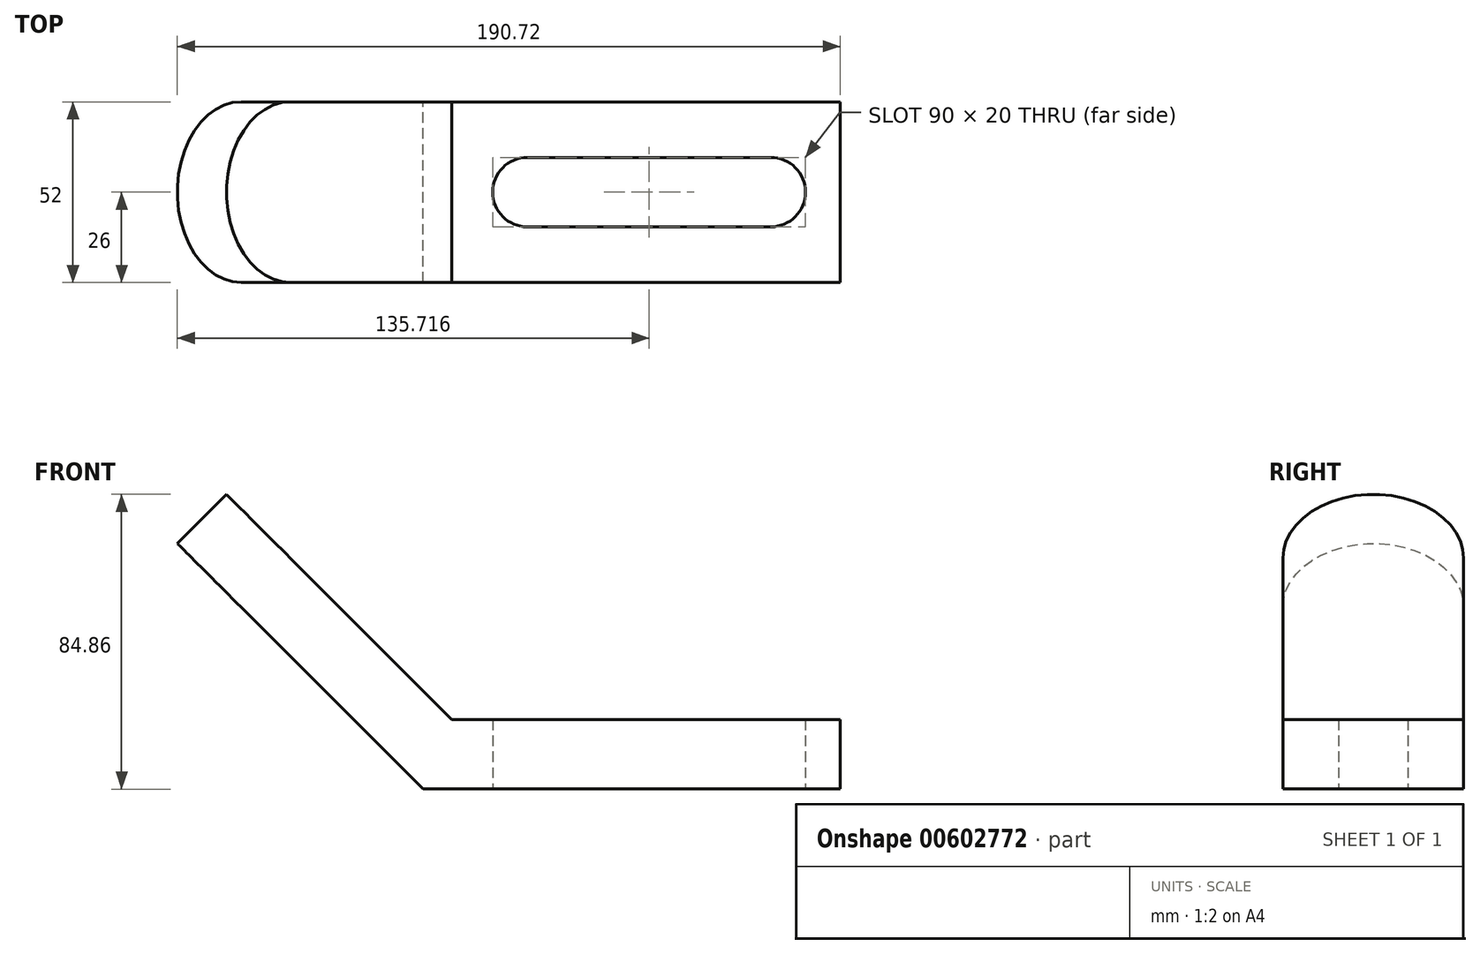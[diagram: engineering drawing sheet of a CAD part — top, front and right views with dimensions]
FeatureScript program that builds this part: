
annotation { "Feature Type Name" : "Feature", "Feature Type Description" : "" }
export const myFeature = defineFeature(function(context is Context, id is Id, definition is map)
    precondition{}
    {
        {
            var Q0;
            Q0=qCreatedBy(makeId("Front.planeOp"),FACE);
            var sketch = newSketch(context, id + "F0", { "sketchPlane" : qUnion([Q0])});
            skLineSegment(sketch, "E0.top", {"start": v(-86.18, 32.88) * mm, "end": v(-156.9, 103.6) * mm});
            skLineSegment(sketch, "E0.right", {"start": v(33.82, 52.88) * mm, "end": v(33.82, 32.88) * mm});
            skLineSegment(sketch, "E1", {"start": v(33.82, 52.88) * mm, "end": v(-77.9, 52.88) * mm});
            skLineSegment(sketch, "E2", {"start": v(-86.18, 32.88) * mm, "end": v(33.82, 32.88) * mm});
            skLineSegment(sketch, "E3", {"start": v(-156.9, 103.6) * mm, "end": v(-142.75, 117.74) * mm});
            skLineSegment(sketch, "E4", {"start": v(-142.75, 117.74) * mm, "end": v(-77.9, 52.88) * mm});
            skSolve(sketch);
        }
        {
            var Q0;
            Q0 = qSketchRegion(id + "F0", true);
            extrude(context, id + "F1", {"entities" : qUnion([Q0]), "depth" : 52 * mm, "offsetDistance" : 25 * mm});
        }
        {
            var Q0;
            Q0=makeQuery(id+"F1.opExtrude","CAP_EDGE",EDGE,{"disambiguationData":[OSD([sQuery(id+"F0.wireOp",EDGE,"E3")])],"isStart":false});
            var Q1;
            Q1=makeQuery(id+"F1.opExtrude","CAP_EDGE",EDGE,{"disambiguationData":[OSD([sQuery(id+"F0.wireOp",EDGE,"E3")])],"isStart":true});
            fillet(context, id + "F2", {"entities" : qUnion([Q0, Q1]), "radius" : 26 * mm, "tangentPropagation" : true, "allowEdgeOverflow" : false});
        }
        {
            var Q0;
            Q0=makeQuery(id+"F1.opExtrude","SWEPT_FACE",FACE,{"disambiguationData":[OSD([sQuery(id+"F0.wireOp",EDGE,"E2")])]});
            var sketch = newSketch(context, id + "F3", { "sketchPlane" : qUnion([Q0])});
            skLineSegment(sketch, "E5.bottom", {"start": v(-56.18, 16) * mm, "end": v(13.82, 16) * mm});
            skLineSegment(sketch, "E5.top", {"start": v(-56.18, 36) * mm, "end": v(13.82, 36) * mm});
            skArc(sketch, "E6", {"start": v(-56.18, 36) * mm, "mid": v(-66.18, 26) * mm, "end": v(-56.18, 16) * mm});
            skPoint(sketch, "E6.third.point", {"position": v(-66.18, 26) * mm});
            skPoint(sketch, "E6.third.point.positionSnap0", {"position": v(-56.18, 26) * mm});
            skArc(sketch, "E7", {"start": v(13.82, 16) * mm, "mid": v(23.82, 26) * mm, "end": v(13.82, 36) * mm});
            skPoint(sketch, "E7.third.point", {"position": v(23.82, 26) * mm});
            skPoint(sketch, "E7.third.point.positionSnap0", {"position": v(13.82, 26) * mm});
            skSolve(sketch);
        }
        {
            var Q0;
            Q0 = qSketchRegion(id + "F3", true);
            extrude(context, id + "F4", {"entities" : qUnion([Q0]), "operationType" : NewBodyOperationType.REMOVE, "oppositeDirection" : true, "depth" : 26 * mm, "offsetDistance" : 25 * mm});
        }
        {
            var Q0;
            Q0=makeQuery(id+"F1.opExtrude","SWEPT_FACE",FACE,{"disambiguationData":[OSD([sQuery(id+"F0.wireOp",EDGE,"E4")])]});
            var sketch = newSketch(context, id + "F5", { "sketchPlane" : qUnion([Q0])});
            skCircle(sketch, "E8", {"center": v(-158.2, -26) * mm, "radius": 10 * mm});
            skSolve(sketch);
        }
        {
            var Q0;
            Q0 = qSketchRegion(id + "F5", true);
            extrude(context, id + "F6", {"entities" : qUnion([Q0]), "operationType" : NewBodyOperationType.REMOVE, "oppositeDirection" : true, "depth" : 25 * mm, "offsetDistance" : 25 * mm});
        }
    });
